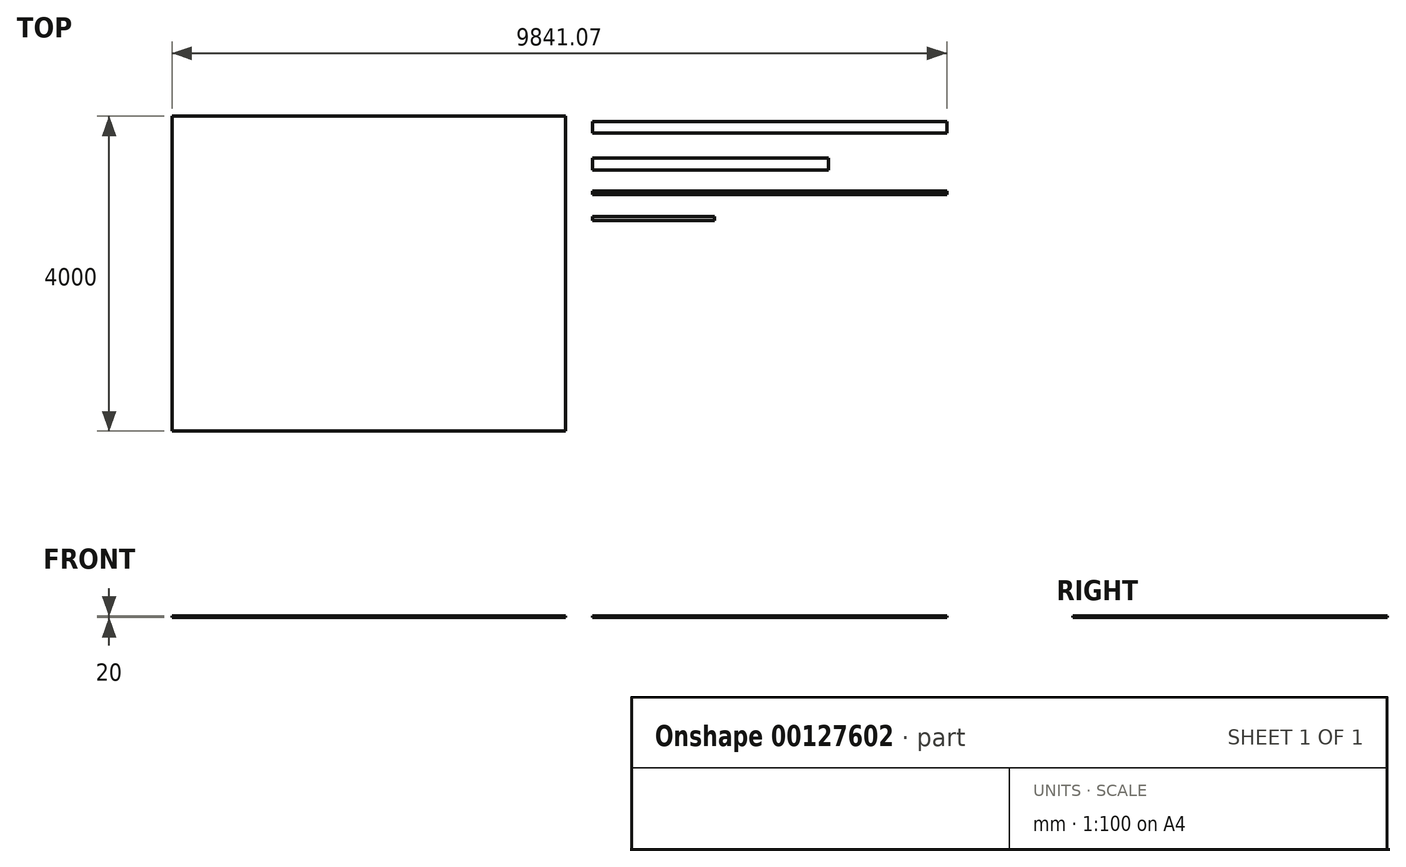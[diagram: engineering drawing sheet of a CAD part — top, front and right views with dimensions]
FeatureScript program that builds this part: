
annotation { "Feature Type Name" : "Feature", "Feature Type Description" : "" }
export const myFeature = defineFeature(function(context is Context, id is Id, definition is map)
    precondition{}
    {
        {
            var Q0;
            Q0=qCreatedBy(makeId("Top.planeOp"),FACE);
            var sketch = newSketch(context, id + "F0", { "sketchPlane" : qUnion([Q0])});
            skLineSegment(sketch, "E0.bottom", {"start": v(-3852.51, 1993.45) * mm, "end": v(1147.49, 1993.45) * mm});
            skLineSegment(sketch, "E0.top", {"start": v(-3852.51, -2006.55) * mm, "end": v(1147.49, -2006.55) * mm});
            skLineSegment(sketch, "E0.left", {"start": v(-3852.51, 1993.45) * mm, "end": v(-3852.51, -2006.55) * mm});
            skLineSegment(sketch, "E0.right", {"start": v(1147.49, 1993.45) * mm, "end": v(1147.49, -2006.55) * mm});
            skLineSegment(sketch, "E1.bottom", {"start": v(1488.56, 1926.66) * mm, "end": v(5988.56, 1926.66) * mm});
            skLineSegment(sketch, "E1.top", {"start": v(1488.56, 1776.66) * mm, "end": v(5988.56, 1776.66) * mm});
            skLineSegment(sketch, "E1.left", {"start": v(1488.56, 1926.66) * mm, "end": v(1488.56, 1776.66) * mm});
            skLineSegment(sketch, "E1.right", {"start": v(5988.56, 1926.66) * mm, "end": v(5988.56, 1776.66) * mm});
            skLineSegment(sketch, "E2.bottom", {"start": v(1488.56, 1459.41) * mm, "end": v(4488.56, 1459.41) * mm});
            skLineSegment(sketch, "E2.top", {"start": v(1488.56, 1309.41) * mm, "end": v(4488.56, 1309.41) * mm});
            skLineSegment(sketch, "E2.left", {"start": v(1488.56, 1459.41) * mm, "end": v(1488.56, 1309.41) * mm});
            skLineSegment(sketch, "E2.right", {"start": v(4488.56, 1459.41) * mm, "end": v(4488.56, 1309.41) * mm});
            skLineSegment(sketch, "E3.bottom", {"start": v(1488.56, 1046.05) * mm, "end": v(5988.56, 1046.05) * mm});
            skLineSegment(sketch, "E3.top", {"start": v(1488.56, 996.05) * mm, "end": v(5988.56, 996.05) * mm});
            skLineSegment(sketch, "E3.left", {"start": v(1488.56, 1046.05) * mm, "end": v(1488.56, 996.05) * mm});
            skLineSegment(sketch, "E3.right", {"start": v(5988.56, 1046.05) * mm, "end": v(5988.56, 996.05) * mm});
            skLineSegment(sketch, "E4.bottom", {"start": v(1488.56, 716.85) * mm, "end": v(3038.56, 716.85) * mm});
            skLineSegment(sketch, "E4.top", {"start": v(1488.56, 666.85) * mm, "end": v(3038.56, 666.85) * mm});
            skLineSegment(sketch, "E4.left", {"start": v(1488.56, 716.85) * mm, "end": v(1488.56, 666.85) * mm});
            skLineSegment(sketch, "E4.right", {"start": v(3038.56, 716.85) * mm, "end": v(3038.56, 666.85) * mm});
            skSolve(sketch);
        }
        {
            var Q0;
            Q0=makeQuery(id+"F0.imprint","IMPRINT",FACE,{"disambiguationData":[TD([[makeQuery(id+"F0.imprint","IMPRINT",EDGE,{"derivedFrom":sQuery(id+"F0.wireOp",EDGE,"E0.bottom")}),-1.0]])]});
            var Q1;
            Q1=makeQuery(id+"F0.imprint","IMPRINT",FACE,{"disambiguationData":[TD([[makeQuery(id+"F0.imprint","IMPRINT",EDGE,{"derivedFrom":sQuery(id+"F0.wireOp",EDGE,"E1.bottom")}),-1.0]])]});
            var Q2;
            Q2=makeQuery(id+"F0.imprint","IMPRINT",FACE,{"disambiguationData":[TD([[makeQuery(id+"F0.imprint","IMPRINT",EDGE,{"derivedFrom":sQuery(id+"F0.wireOp",EDGE,"E2.bottom")}),-1.0]])]});
            var Q3;
            Q3=makeQuery(id+"F0.imprint","IMPRINT",FACE,{"disambiguationData":[TD([[makeQuery(id+"F0.imprint","IMPRINT",EDGE,{"derivedFrom":sQuery(id+"F0.wireOp",EDGE,"E3.bottom")}),-1.0]])]});
            var Q4;
            Q4=makeQuery(id+"F0.imprint","IMPRINT",FACE,{"disambiguationData":[TD([[makeQuery(id+"F0.imprint","IMPRINT",EDGE,{"derivedFrom":sQuery(id+"F0.wireOp",EDGE,"E4.bottom")}),-1.0]])]});
            extrude(context, id + "F1", {"entities" : qUnion([Q0, Q1, Q2, Q3, Q4]), "depth" : 20 * mm});
        }
    });
